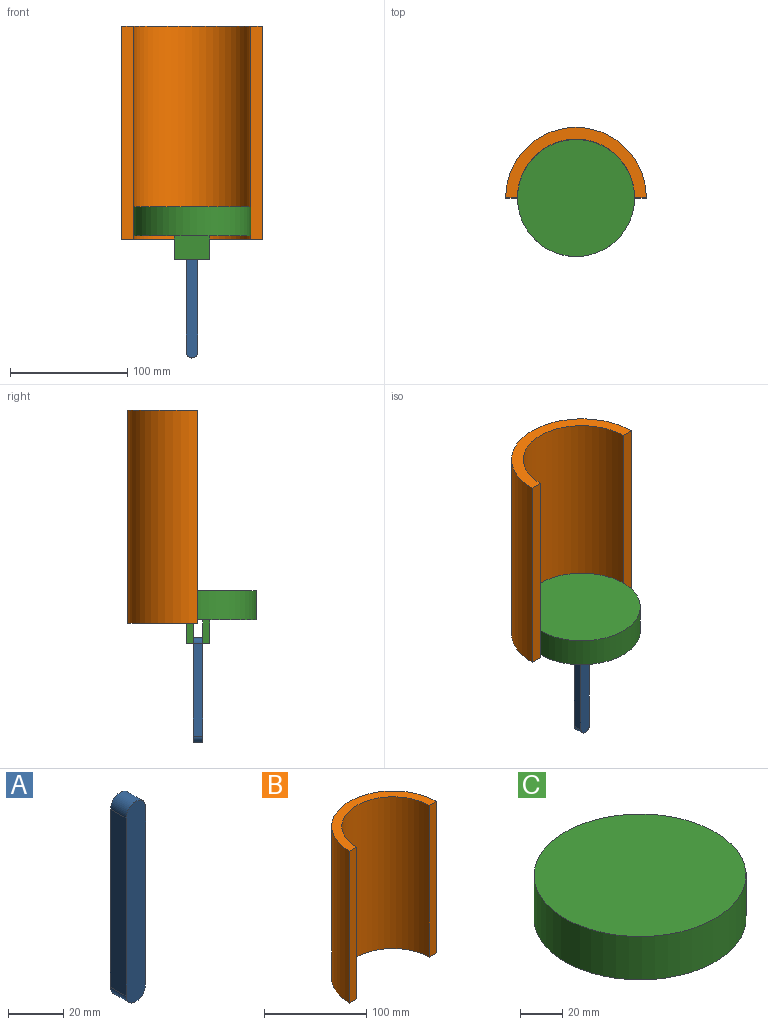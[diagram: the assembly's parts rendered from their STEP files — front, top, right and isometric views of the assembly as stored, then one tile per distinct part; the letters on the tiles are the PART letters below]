
ASSEMBLY  parts=3 mates=2
PART A: 6 faces, bbox 10x8x89.2 mm
  f0: cylinder r=5mm len=10mm, axis (0,1,0), area 125.7mm2, adj f1,f3,f4,f5
  f1: plane 79.19x8mm, normal (1,0,0), area 633.5mm2, adj f0,f2,f4,f5
  f2: cylinder r=5mm len=10mm, axis (0,1,0), area 125.7mm2, adj f1,f3,f4,f5
  f3: plane 79.19x8mm, normal (-1,0,0), area 633.5mm2, adj f0,f2,f4,f5
  f4: plane 89.19x10mm, normal (0,-1,0), area 870.5mm2, adj f0,f1,f2,f3
  f5: plane 89.19x10mm, normal (0,1,0), area 870.5mm2, adj f0,f1,f2,f3
PART B: 6 faces, bbox 120x60x182 mm
  f0: cylinder r=50mm len=182mm, axis (0,0,-1), area 28588.5mm2, adj f1,f3,f4,f5
  f1: plane 182x10mm, normal (0,-1,0), area 1820mm2, adj f0,f2,f4,f5
  f2: cylinder r=60mm len=182mm, axis (0,0,-1), area 34306.2mm2, adj f1,f3,f4,f5
  f3: plane 182x10mm, normal (0,-1,0), area 1820mm2, adj f0,f2,f4,f5
  f4: plane 120x60mm, normal (0,0,1), area 1727.9mm2, adj f0,f1,f2,f3
  f5: plane 120x60mm, normal (0,0,-1), area 1727.9mm2, adj f0,f1,f2,f3
PART C: 13 faces, bbox 100x100x45 mm
  f0: cylinder r=50mm len=100mm, axis (0,0,-1), area 7854mm2, adj f1,f2
  f1: plane 100x100mm, normal (0,0,1), area 7854mm2, adj f0
  f2: plane 100x100mm, normal (0,0,-1), area 7494mm2, adj f0,f3,f4,f5,f6,f8,f9,f10
  f3: plane 20x6mm, normal (1,0,0), area 120mm2, adj f2,f4,f6,f7
  f4: plane 30x20mm, normal (0,-1,0), area 600mm2, adj f2,f3,f5,f7
  f5: plane 20x6mm, normal (-1,0,0), area 120mm2, adj f2,f4,f6,f7
  f6: plane 30x20mm, normal (0,1,0), area 600mm2, adj f2,f3,f5,f7
  f7: plane 30x6mm, normal (0,0,-1), area 180mm2, adj f3,f4,f5,f6
  f8: plane 20x6mm, normal (1,0,0), area 120mm2, adj f2,f9,f11,f12
  f9: plane 30x20mm, normal (0,-1,0), area 600mm2, adj f2,f8,f10,f12
  f10: plane 20x6mm, normal (-1,0,0), area 120mm2, adj f2,f9,f11,f12
  f11: plane 30x20mm, normal (0,1,0), area 600mm2, adj f2,f8,f10,f12
  f12: plane 30x6mm, normal (0,0,-1), area 180mm2, adj f8,f9,f10,f11
PLACE A rot(axis=(0,0,1),180deg) t=(0,-14,2.75)mm
PLACE B at identity fixed
PLACE C t=(0,0,2.75)mm
MATE revolute A.f2 <-> C.f9  axis (0,1,0) through (0,4,-17.25)mm
MATE slider C.f0 <-> B.f0  axis (0,0,1) through (0,0,27.75)mm
